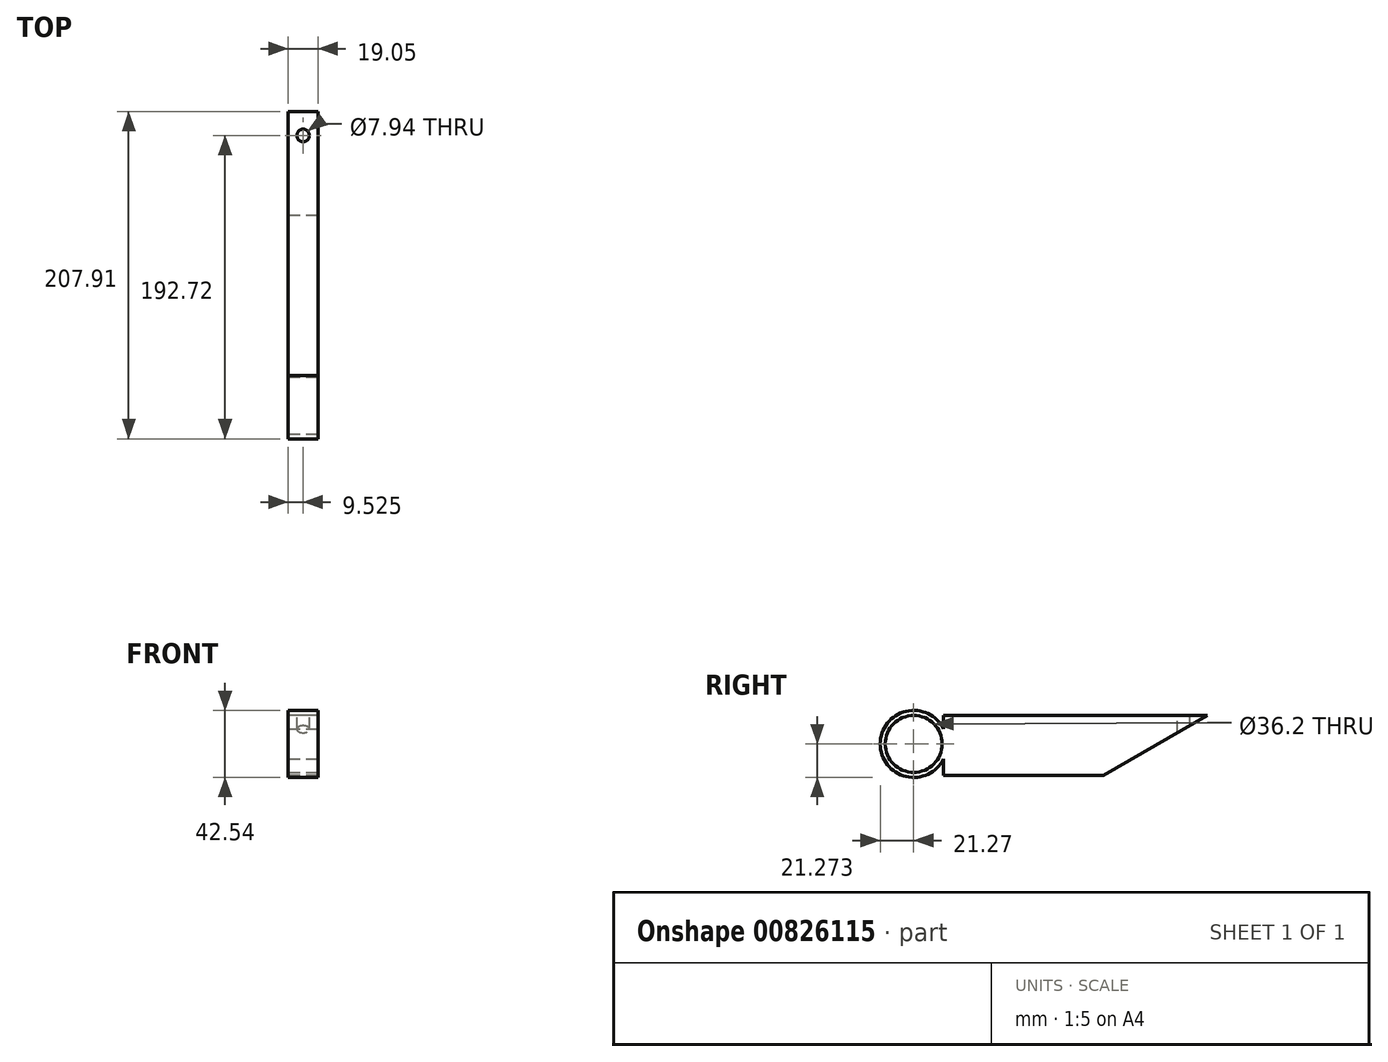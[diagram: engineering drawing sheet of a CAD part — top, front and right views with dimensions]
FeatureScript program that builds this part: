
annotation { "Feature Type Name" : "Feature", "Feature Type Description" : "" }
export const myFeature = defineFeature(function(context is Context, id is Id, definition is map)
    precondition{}
    {
        {
            var Q0;
            Q0=qCreatedBy(makeId("Front.planeOp"),FACE);
            var sketch = newSketch(context, id + "F0", { "sketchPlane" : qUnion([Q0])});
            skLineSegment(sketch, "E0.bottom", {"start": v(0, 0) * mm, "end": v(19.05, 0) * mm});
            skLineSegment(sketch, "E0.top", {"start": v(0, 38.1) * mm, "end": v(19.05, 38.1) * mm});
            skLineSegment(sketch, "E0.left", {"start": v(0, 0) * mm, "end": v(0, 38.1) * mm});
            skLineSegment(sketch, "E0.right", {"start": v(19.05, 0) * mm, "end": v(19.05, 38.1) * mm});
            skSolve(sketch);
        }
        {
            var Q0;
            Q0=qSketchRegion(id+"F0",true);
            extrude(context, id + "F1", {"entities" : qUnion([Q0]), "endBound" : BoundingType.SYMMETRIC, "depth" : 254 * mm, "offsetDistance" : 25.4 * mm});
        }
        {
            var Q0;
            Q0=makeQuery(id+"F1.opExtrude","SWEPT_FACE",FACE,{"disambiguationData":[OSD([sQuery(id+"F0.wireOp",EDGE,"E0.right")])]});
            var sketch = newSketch(context, id + "F2", { "sketchPlane" : qUnion([Q0])});
            skCircle(sketch, "E1", {"center": v(-146.05, 20) * mm, "radius": 21.27 * mm});
            skCircle(sketch, "E2", {"center": v(-146.05, 20) * mm, "radius": 18.1 * mm});
            skSolve(sketch);
        }
        {
            var Q0;
            Q0=makeQuery(id+"F2.imprint","IMPRINT",FACE,{"disambiguationData":[TD([[makeQuery(id+"F2.imprint","IMPRINT",EDGE,{"derivedFrom":sQuery(id+"F2.wireOp",EDGE,"E2")}),-1.0]])]});
            extrude(context, id + "F3", {"entities" : qUnion([Q0]), "oppositeDirection" : true, "depth" : 19.05 * mm, "offsetDistance" : 25.4 * mm});
        }
        {
            var Q0;
            Q0=makeQuery(id+"F3.opExtrude","SWEPT_BODY",BODY,{"disambiguationData":[OSD([sQuery(id+"F0.wireOp",EDGE,"E0.right"),sQuery(id+"F2.wireOp",EDGE,"E1"),sQuery(id+"F2.wireOp",EDGE,"E2")])]});
            var Q1;
            Q1=makeQuery(id+"F1.opExtrude","SWEPT_BODY",BODY,{"disambiguationData":[OSD([sQuery(id+"F0.wireOp",EDGE,"E0.bottom"),sQuery(id+"F0.wireOp",EDGE,"E0.top"),sQuery(id+"F0.wireOp",EDGE,"E0.left"),sQuery(id+"F0.wireOp",EDGE,"E0.right")])]});
            booleanBodies(context, id + "F4", {"operationType" : BooleanOperationType.UNION, "tools" : qUnion([Q0, Q1])});
        }
        {
            var Q0;
            Q0=makeQuery(id+"F1.opExtrude","SWEPT_FACE",FACE,{"disambiguationData":[OSD([sQuery(id+"F0.wireOp",EDGE,"E0.top")])]});
            var sketch = newSketch(context, id + "F5", { "sketchPlane" : qUnion([Q0])});
            skCircle(sketch, "E3", {"center": v(9.53, 25.4) * mm, "radius": 3.97 * mm});
            skSolve(sketch);
        }
        {
            var Q0;
            Q0=makeQuery(id+"F5.imprint","IMPRINT",FACE,{"disambiguationData":[TD([[makeQuery(id+"F5.imprint","IMPRINT",EDGE,{"derivedFrom":sQuery(id+"F5.wireOp",EDGE,"E3")}),1.0]])]});
            extrude(context, id + "F6", {"entities" : qUnion([Q0]), "operationType" : NewBodyOperationType.REMOVE, "endBound" : BoundingType.THROUGH_ALL, "oppositeDirection" : true, "depth" : 25.4 * mm, "offsetDistance" : 25.4 * mm});
        }
        {
            var Q0;
            Q0=makeQuery(id+"F4.opBoolean","MERGE",FACE,{"derivedFrom":[makeQuery(id+"F1.opExtrude","SWEPT_FACE",FACE,{"disambiguationData":[OSD([sQuery(id+"F0.wireOp",EDGE,"E0.left")])]}),makeQuery(id+"F3.opExtrude","CAP_FACE",FACE,{"disambiguationData":[OSD([sQuery(id+"F0.wireOp",EDGE,"E0.right"),sQuery(id+"F2.wireOp",EDGE,"E1"),sQuery(id+"F2.wireOp",EDGE,"E2")])],"isStart":false})]});
            var sketch = newSketch(context, id + "F7", { "sketchPlane" : qUnion([Q0])});
            skLineSegment(sketch, "E4", {"start": v(25.4, 0) * mm, "end": v(-40.6, 38.1) * mm});
            skLineSegment(sketch, "E5", {"start": v(-40.6, 38.1) * mm, "end": v(25.4, 0) * mm});
            skLineSegment(sketch, "E6", {"start": v(25.4, 0) * mm, "end": v(-127, 0) * mm});
            skLineSegment(sketch, "E7", {"start": v(-127, 0) * mm, "end": v(-127, 38.1) * mm});
            skLineSegment(sketch, "E8", {"start": v(-127, 38.1) * mm, "end": v(-40.6, 38.1) * mm});
            skSolve(sketch);
        }
        {
            var Q0;
            Q0 = qSketchRegion(id + "F7", true);
            extrude(context, id + "F8", {"entities" : qUnion([Q0]), "operationType" : NewBodyOperationType.REMOVE, "endBound" : BoundingType.THROUGH_ALL, "oppositeDirection" : true, "depth" : 25.4 * mm, "offsetDistance" : 25.4 * mm});
        }
    });
